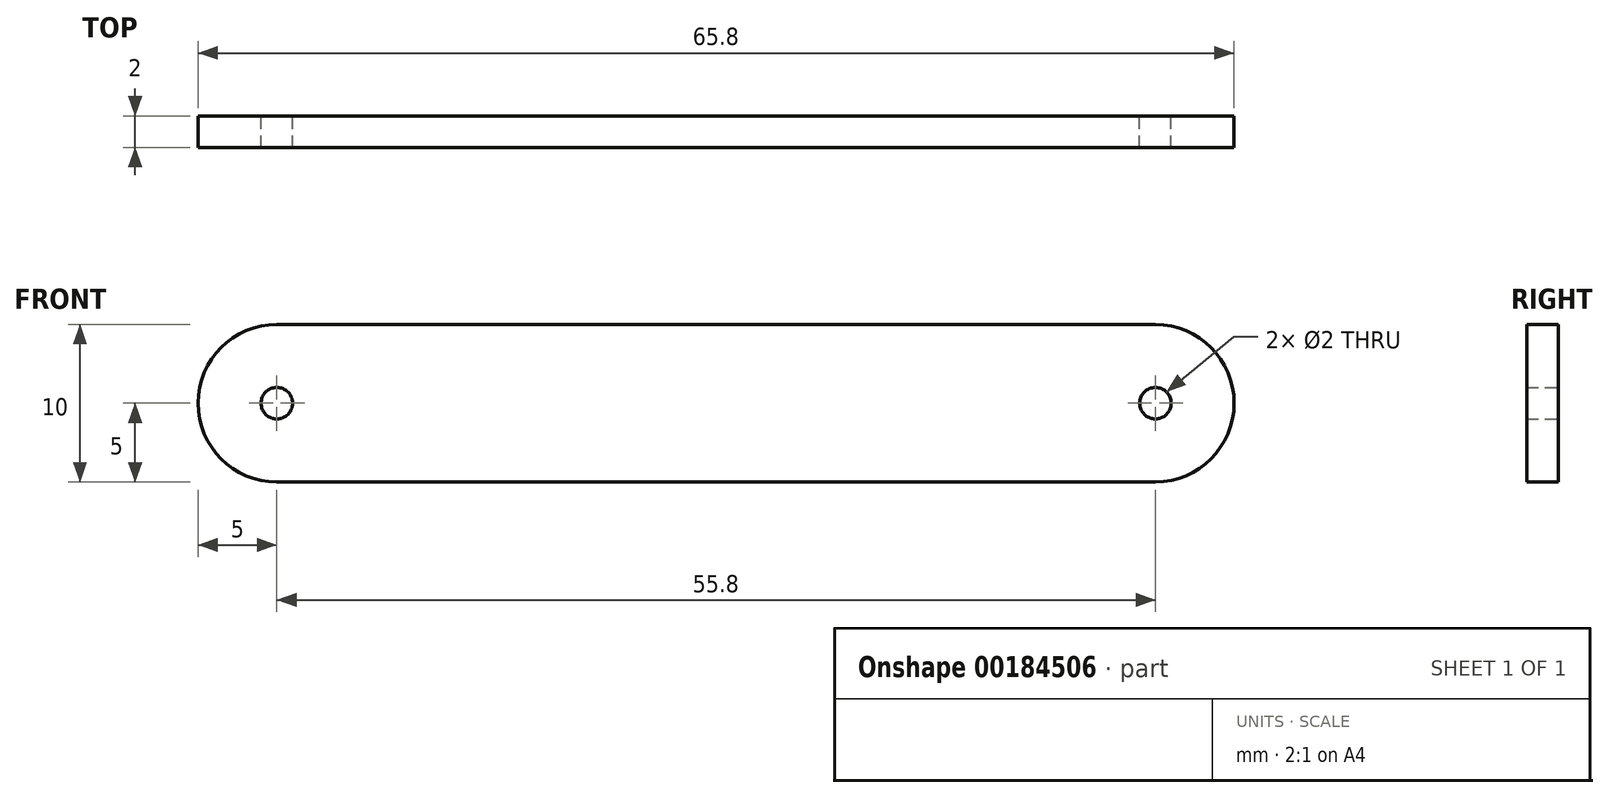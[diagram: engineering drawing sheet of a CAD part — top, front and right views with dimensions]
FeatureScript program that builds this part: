
annotation { "Feature Type Name" : "Feature", "Feature Type Description" : "" }
export const myFeature = defineFeature(function(context is Context, id is Id, definition is map)
    precondition{}
    {
        {
            var Q0;
            Q0=qCreatedBy(makeId("Front.planeOp"),FACE);
            var sketch = newSketch(context, id + "F0", { "sketchPlane" : qUnion([Q0])});
            skLineSegment(sketch, "E0.bottom", {"start": v(0, 0) * mm, "end": v(65.8, 0) * mm});
            skLineSegment(sketch, "E0.top", {"start": v(0, -10) * mm, "end": v(65.8, -10) * mm});
            skLineSegment(sketch, "E0.left", {"start": v(0, 0) * mm, "end": v(0, -10) * mm});
            skLineSegment(sketch, "E0.right", {"start": v(65.8, 0) * mm, "end": v(65.8, -10) * mm});
            skCircle(sketch, "E1", {"center": v(5, -5) * mm, "radius": 1 * mm});
            skCircle(sketch, "E2", {"center": v(60.8, -5) * mm, "radius": 1 * mm});
            skPoint(sketch, "E2.centerSnap0", {"position": v(0, -5) * mm});
            skSolve(sketch);
        }
        {
            var Q0;
            Q0 = qSketchRegion(id + "F0", true);
            extrude(context, id + "F1", {"entities" : qUnion([Q0]), "depth" : 2 * mm});
        }
        {
            var Q0;
            Q0=makeQuery(id+"F1.opExtrude","SWEPT_EDGE",EDGE,{"disambiguationData":[OSD([sQuery(id+"F0.wireOp",EDGE,"E0.bottom"),sQuery(id+"F0.wireOp",EDGE,"E0.left")])]});
            var Q1;
            Q1=makeQuery(id+"F1.opExtrude","SWEPT_EDGE",EDGE,{"disambiguationData":[OSD([sQuery(id+"F0.wireOp",EDGE,"E0.top"),sQuery(id+"F0.wireOp",EDGE,"E0.left")])]});
            var Q2;
            Q2=makeQuery(id+"F1.opExtrude","SWEPT_EDGE",EDGE,{"disambiguationData":[OSD([sQuery(id+"F0.wireOp",EDGE,"E0.bottom"),sQuery(id+"F0.wireOp",EDGE,"E0.right")])]});
            var Q3;
            Q3=makeQuery(id+"F1.opExtrude","SWEPT_EDGE",EDGE,{"disambiguationData":[OSD([sQuery(id+"F0.wireOp",EDGE,"E0.top"),sQuery(id+"F0.wireOp",EDGE,"E0.right")])]});
            fillet(context, id + "F2", {"entities" : qUnion([Q0, Q1, Q2, Q3]), "radius" : 5 * mm, "tangentPropagation" : true, "allowEdgeOverflow" : false});
        }
    });
